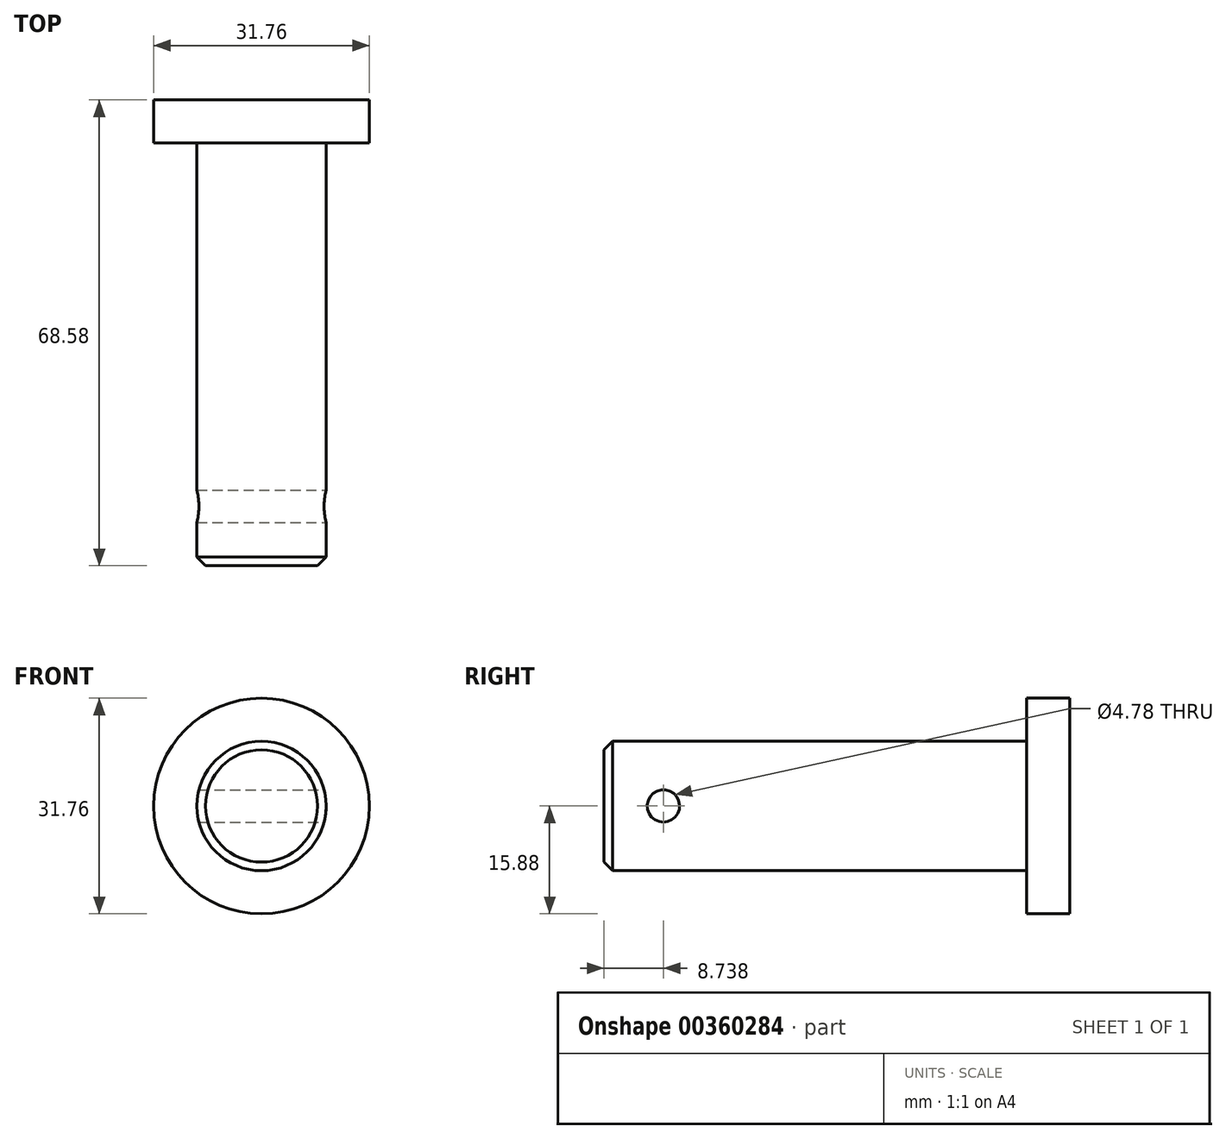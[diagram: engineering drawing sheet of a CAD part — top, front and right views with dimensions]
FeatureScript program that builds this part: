
annotation { "Feature Type Name" : "Feature", "Feature Type Description" : "" }
export const myFeature = defineFeature(function(context is Context, id is Id, definition is map)
    precondition{}
    {
        {
            var Q0;
            Q0=qCreatedBy(makeId("Front.planeOp"),FACE);
            var sketch = newSketch(context, id + "F0", { "sketchPlane" : qUnion([Q0])});
            skCircle(sketch, "E0", {"center": v(0, 0) * mm, "radius": 15.87 * mm});
            skSolve(sketch);
        }
        {
            var Q0;
            Q0=makeQuery(id+"F0.imprint","IMPRINT",FACE,{"disambiguationData":[TD([[makeQuery(id+"F0.imprint","IMPRINT",EDGE,{"derivedFrom":sQuery(id+"F0.wireOp",EDGE,"E0")}),1.0]])]});
            extrude(context, id + "F1", {"entities" : qUnion([Q0]), "depth" : 6.35 * mm});
        }
        {
            var Q0;
            Q0=makeQuery(id+"F1.opExtrude","CAP_FACE",FACE,{"disambiguationData":[OSD([sQuery(id+"F0.wireOp",EDGE,"E0")])],"isStart":false});
            var sketch = newSketch(context, id + "F2", { "sketchPlane" : qUnion([Q0])});
            skCircle(sketch, "E1", {"center": v(0, 0) * mm, "radius": 9.53 * mm});
            skSolve(sketch);
        }
        {
            var Q0;
            Q0 = qSketchRegion(id + "F2", true);
            extrude(context, id + "F3", {"entities" : qUnion([Q0]), "operationType" : NewBodyOperationType.ADD, "depth" : 62.23 * mm});
        }
        {
            var Q0;
            Q0=qCreatedBy(makeId("Right.planeOp"),FACE);
            var sketch = newSketch(context, id + "F4", { "sketchPlane" : qUnion([Q0])});
            skLineSegment(sketch, "E2", {"start": v(0, 0) * mm, "end": v(-68.58, 0) * mm, "construction": true});
            skCircle(sketch, "E3", {"center": v(-59.84, 0) * mm, "radius": 2.39 * mm});
            skSolve(sketch);
        }
        {
            var Q0;
            Q0 = qSketchRegion(id + "F4", true);
            extrude(context, id + "F5", {"entities" : qUnion([Q0]), "operationType" : NewBodyOperationType.REMOVE, "oppositeDirection" : true, "depth" : 127 * mm, "symmetric" : true});
        }
        {
            var Q0;
            Q0=makeQuery(id+"F3.opExtrude","CAP_EDGE",EDGE,{"disambiguationData":[OSD([sQuery(id+"F2.wireOp",EDGE,"E1")])],"isStart":false});
            chamfer(context, id + "F6", {"entities" : qUnion([Q0]), "width" : 1.27 * mm, "tangentPropagation" : true});
        }
    });
